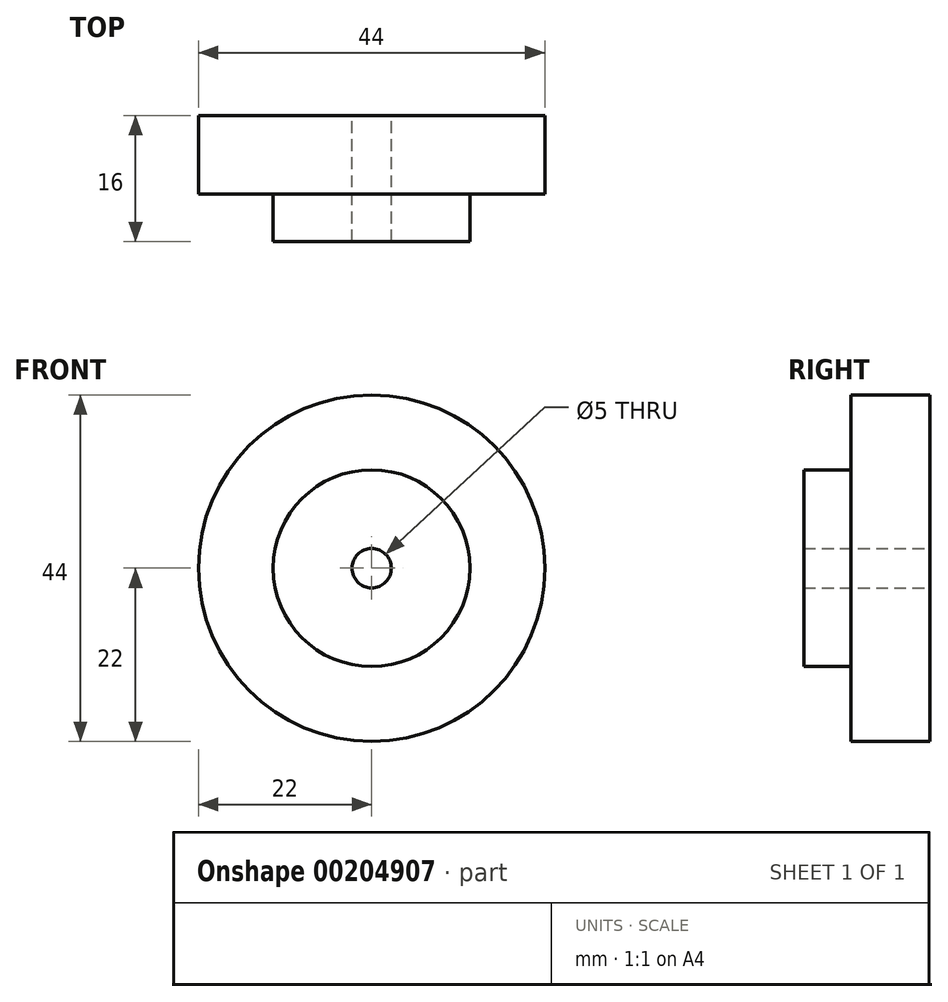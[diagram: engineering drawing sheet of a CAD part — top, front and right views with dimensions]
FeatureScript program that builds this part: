
annotation { "Feature Type Name" : "Feature", "Feature Type Description" : "" }
export const myFeature = defineFeature(function(context is Context, id is Id, definition is map)
    precondition{}
    {
        {
            var Q0;
            Q0=qCreatedBy(makeId("Front.planeOp"),FACE);
            var sketch = newSketch(context, id + "F0", { "sketchPlane" : qUnion([Q0])});
            skCircle(sketch, "E0", {"center": v(0, 0) * mm, "radius": 12.5 * mm});
            skCircle(sketch, "E1", {"center": v(0, 0) * mm, "radius": 22 * mm});
            skCircle(sketch, "E2", {"center": v(0, 0) * mm, "radius": 2.5 * mm});
            skSolve(sketch);
        }
        {
            var Q0;
            Q0=makeQuery(id+"F0.imprint","IMPRINT",FACE,{"disambiguationData":[TD([[makeQuery(id+"F0.imprint","IMPRINT",EDGE,{"derivedFrom":sQuery(id+"F0.wireOp",EDGE,"E0")}),1.0]])]});
            extrude(context, id + "F1", {"entities" : qUnion([Q0]), "depth" : 6 * mm});
        }
        {
            var Q0;
            Q0=makeQuery(id+"F0.imprint","IMPRINT",FACE,{"disambiguationData":[TD([[makeQuery(id+"F0.imprint","IMPRINT",EDGE,{"derivedFrom":sQuery(id+"F0.wireOp",EDGE,"E0")}),1.0]])]});
            var Q1;
            Q1=makeQuery(id+"F0.imprint","IMPRINT",FACE,{"disambiguationData":[TD([[makeQuery(id+"F0.imprint","IMPRINT",EDGE,{"derivedFrom":sQuery(id+"F0.wireOp",EDGE,"E0")}),-1.0]])]});
            extrude(context, id + "F2", {"entities" : qUnion([Q0, Q1]), "operationType" : NewBodyOperationType.ADD, "oppositeDirection" : true, "depth" : 10 * mm});
        }
    });
